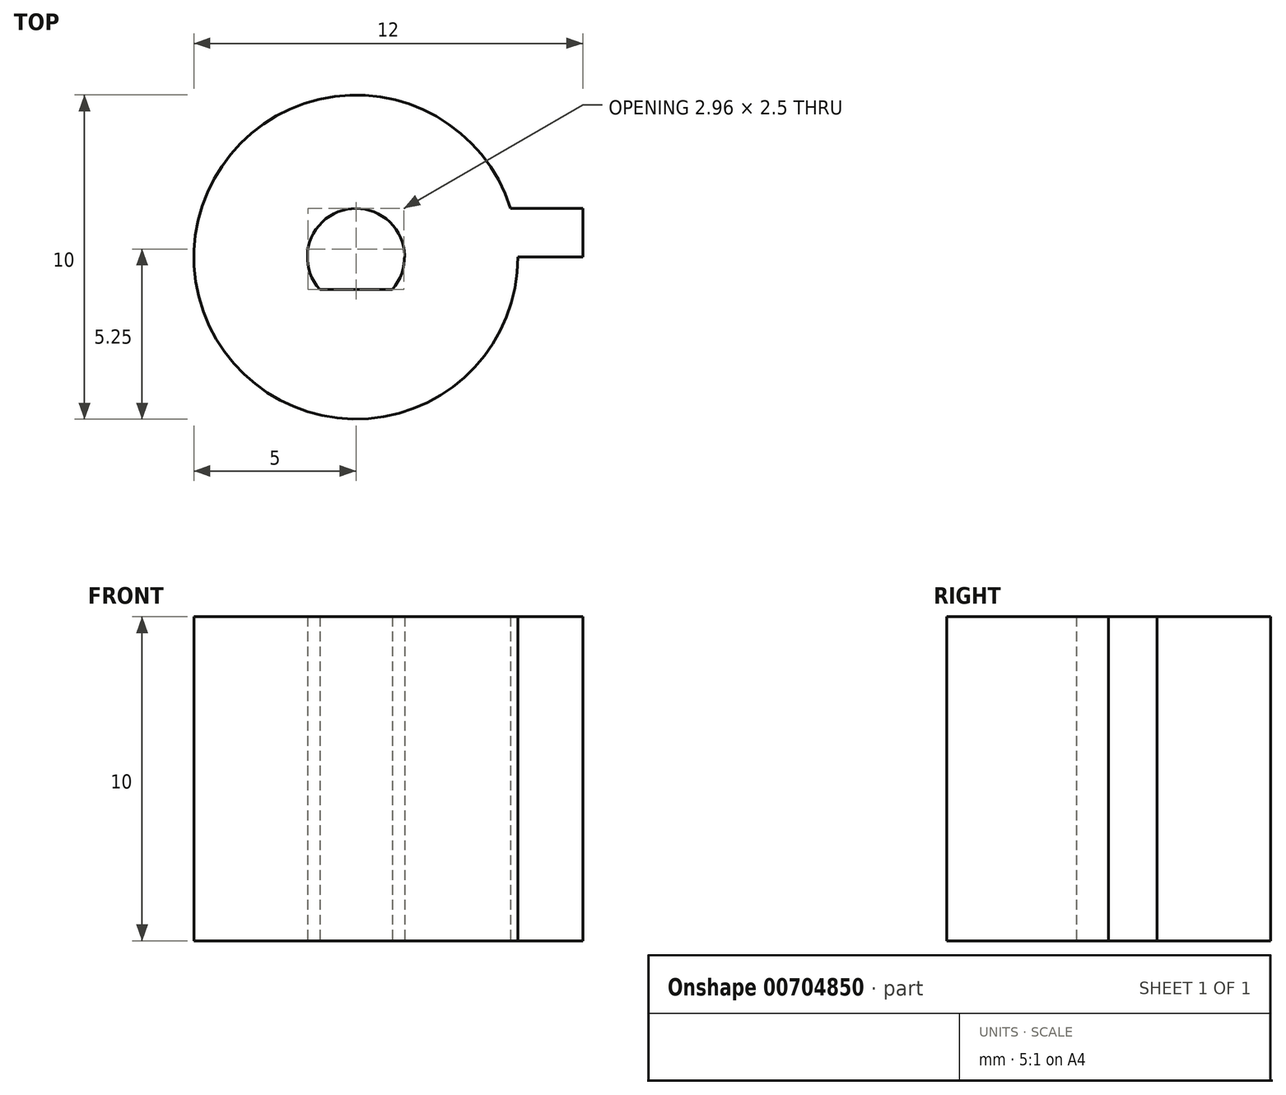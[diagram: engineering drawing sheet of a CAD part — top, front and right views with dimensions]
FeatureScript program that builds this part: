
annotation { "Feature Type Name" : "Feature", "Feature Type Description" : "" }
export const myFeature = defineFeature(function(context is Context, id is Id, definition is map)
    precondition{}
    {
        {
            var Q0;
            Q0=qCreatedBy(makeId("Top.planeOp"),FACE);
            var sketch = newSketch(context, id + "F0", { "sketchPlane" : qUnion([Q0])});
            skArc(sketch, "E0", {"start": v(1.12, -1) * mm, "mid": v(0, 1.5) * mm, "end": v(-1.12, -1) * mm});
            skLineSegment(sketch, "E1", {"start": v(0, 1.5) * mm, "end": v(0, -1) * mm, "construction": true});
            skLineSegment(sketch, "E2", {"start": v(0, -1) * mm, "end": v(-1.12, -1) * mm});
            skLineSegment(sketch, "E3", {"start": v(0, -1) * mm, "end": v(1.12, -1) * mm});
            skArc(sketch, "E4", {"start": v(4.77, 1.5) * mm, "mid": v(-4.94, -0.76) * mm, "end": v(5, 0) * mm});
            skLineSegment(sketch, "E5.bottom", {"start": v(4.77, 1.5) * mm, "end": v(7, 1.5) * mm});
            skLineSegment(sketch, "E5.top", {"start": v(5, 0) * mm, "end": v(7, 0) * mm});
            skLineSegment(sketch, "E5.left", {"start": v(0, 1.5) * mm, "end": v(0, 0) * mm, "construction": true});
            skLineSegment(sketch, "E5.right", {"start": v(7, 1.5) * mm, "end": v(7, 0) * mm});
            skSolve(sketch);
        }
        {
            var Q0;
            Q0=makeQuery(id+"F0.imprint","IMPRINT",FACE,{"disambiguationData":[TD([[makeQuery(id+"F0.imprint","IMPRINT",EDGE,{"derivedFrom":sQuery(id+"F0.wireOp",EDGE,"E0")}),-1.0]])]});
            extrude(context, id + "F1", {"entities" : qUnion([Q0]), "depth" : 10 * mm, "offsetDistance" : 25 * mm});
        }
        {
            var Q0;
            Q0=makeQuery(id+"F0.imprint","IMPRINT",FACE,{"disambiguationData":[TD([[makeQuery(id+"F0.imprint","IMPRINT",EDGE,{"derivedFrom":sQuery(id+"F0.wireOp",EDGE,"E0")}),-1.0]])]});
            extrude(context, id + "F2", {"entities" : qUnion([Q0]), "operationType" : NewBodyOperationType.ADD, "depth" : 10 * mm, "offsetDistance" : 25 * mm});
        }
    });
